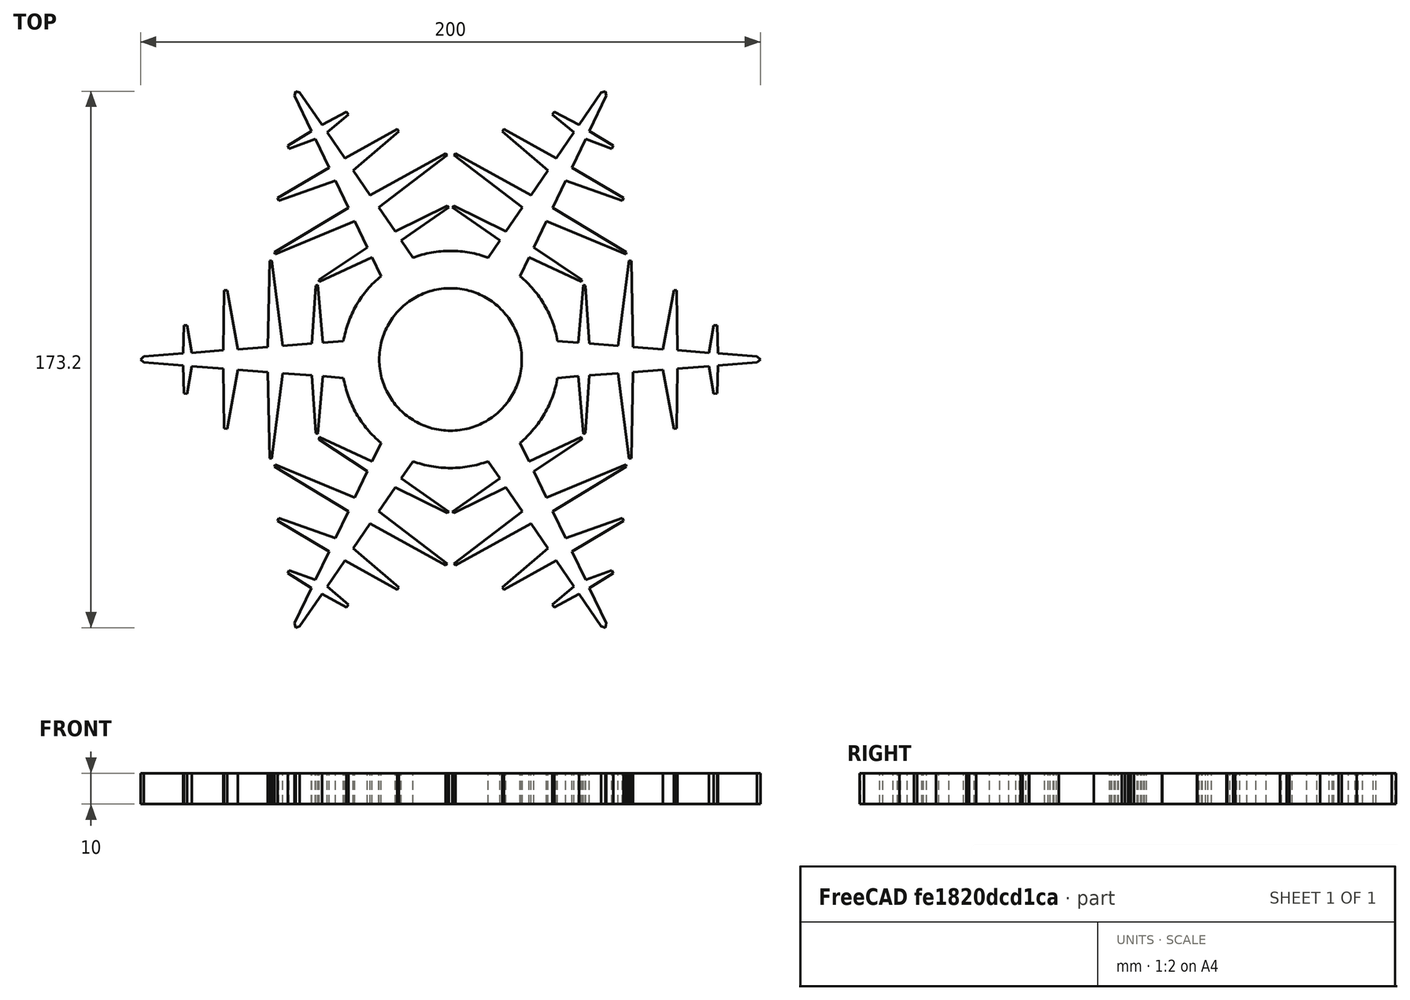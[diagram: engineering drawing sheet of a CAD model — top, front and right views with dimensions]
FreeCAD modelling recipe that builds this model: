
FCSTD DOCUMENT  (FreeCAD 0.17R13541 (Git))
Label: SkiBaskets1
License: All rights reserved
LicenseURL: http://en.wikipedia.org/wiki/All_rights_reserved
objects: Sketcher::SketchObject×1, PartDesign::Pad×1, PartDesign::Mirrored×1, PartDesign::PolarPattern×1, PartDesign::MultiTransform×1, PartDesign::Body×1
note: 7 computed .brp shape members not serialized (recipe doc carries the construction recipe); baked Part::Feature solids carry a one-line shape summary decoded from their .brp

FEATURE [Sketcher::SketchObject] Sketch
  MapMode = 5
  Support = -> [XY_Plane]
  sketch-geometry (25):
    g0: LineSegment [constr] StartX=0 StartY=0 StartZ=0 EndX=60.6218 EndY=35 EndZ=0
    g1: LineSegment [constr] StartX=60.6218 StartY=35 StartZ=0 EndX=100 EndY=0 EndZ=0
    g2: LineSegment StartX=34.54 StartY=5.95197 StartZ=0 EndX=41.2232 EndY=5.43352 EndZ=0
    g3: LineSegment StartX=41.2232 StartY=5.43352 StartZ=0 EndX=42.8555 EndY=24.0849 EndZ=0
    g4: LineSegment StartX=42.8555 StartY=24.0849 StartZ=0 EndX=43.5365 EndY=23.8475 EndZ=0
    g5: LineSegment StartX=43.5365 StartY=23.8475 StartZ=0 EndX=44.7202 EndY=5.16224 EndZ=0
    g6: LineSegment StartX=44.7202 StartY=5.16224 StartZ=0 EndX=54.1123 EndY=4.43366 EndZ=0
    g7: LineSegment StartX=54.1123 StartY=4.43366 StartZ=0 EndX=57.6624 EndY=32.01 EndZ=0
    g8: LineSegment StartX=57.6624 StartY=32.01 StartZ=0 EndX=58.3815 EndY=31.8584 EndZ=0
    g9: LineSegment StartX=58.3815 StartY=31.8584 StartZ=0 EndX=58.9305 EndY=4.05989 EndZ=0
    g10: LineSegment StartX=58.9305 StartY=4.05989 StartZ=0 EndX=68.574 EndY=3.31181 EndZ=0
    g11: LineSegment StartX=68.574 StartY=3.31181 StartZ=0 EndX=72.0968 EndY=22.3422 EndZ=0
    g12: LineSegment StartX=72.0968 StartY=22.3422 StartZ=0 EndX=73.036 EndY=22.2997 EndZ=0
    g13: LineSegment StartX=73.036 StartY=22.2997 StartZ=0 EndX=73.2706 EndY=2.94747 EndZ=0
    g14: LineSegment StartX=73.2706 StartY=2.94747 StartZ=0 EndX=83.4211 EndY=2.16006 EndZ=0
    g15: LineSegment StartX=83.4211 StartY=2.16006 StartZ=0 EndX=84.9667 EndY=11.0606 EndZ=0
    g16: LineSegment StartX=84.9667 StartY=11.0606 StartZ=0 EndX=86.0776 EndY=10.9646 EndZ=0
    g17: LineSegment StartX=86.0776 StartY=10.9646 StartZ=0 EndX=86.3302 EndY=1.93438 EndZ=0
    g18: LineSegment StartX=86.3302 StartY=1.93438 StartZ=0 EndX=98.9227 EndY=0.957527 EndZ=0
    g19: LineSegment StartX=98.9227 StartY=0.957527 StartZ=0 EndX=100 EndY=0 EndZ=0
    g20: LineSegment StartX=100 StartY=0 StartZ=0 EndX=23 EndY=0 EndZ=0
    g21: LineSegment [constr] StartX=30.3743 StartY=6.27512 StartZ=0 EndX=98.9227 EndY=0.957527 EndZ=0
    g22: ArcOfCircle CenterX=0 CenterY=0 CenterZ=0 NormalX=0 NormalY=0 NormalZ=1 AngleXU=0 Radius=23 StartAngle=0 EndAngle=1.5708
    g23: ArcOfCircle CenterX=0 CenterY=0 CenterZ=0 NormalX=0 NormalY=0 NormalZ=1 AngleXU=0 Radius=35.049 StartAngle=0.170645 EndAngle=1.5708
    g24: LineSegment StartX=0 StartY=23 StartZ=0 EndX=0 EndY=35.049 EndZ=0
  constraints (50):
    c: Coincident(g0,g-1)
    c: DistanceX(g-1,g1) = 100
    c: Angle(g-1,g0) = 0.523599
    c: Coincident(g1,g0)
    c: Distance(g0) = 70
    c: Coincident(g3,g2)
    c: Coincident(g4,g3)
    c: Coincident(g5,g4)
    c: Coincident(g6,g5)
    c: Coincident(g7,g6)
    c: Coincident(g8,g7)
    c: Coincident(g9,g8)
    c: Coincident(g10,g9)
    c: Coincident(g12,g11)
    c: Coincident(g13,g12)
    c: Coincident(g14,g13)
    c: Coincident(g15,g14)
    c: Coincident(g16,g15)
    c: Coincident(g17,g16)
    c: Coincident(g18,g17)
    c: Coincident(g19,g18)
    c: Coincident(g21,g18)
    c: PointOnObject(g18,g1)
    c: PointOnObject(g17,g21)
    c: PointOnObject(g14,g21)
    c: PointOnObject(g13,g21)
    c: PointOnObject(g10,g21)
    c: Coincident(g11,g10)
    c: PointOnObject(g9,g21)
    c: PointOnObject(g6,g21)
    c: PointOnObject(g5,g21)
    c: PointOnObject(g2,g21)
    c: PointOnObject(g2,g21)
    c: Equal(g15,g17)
    c: Equal(g13,g11)
    c: Equal(g9,g7)
    c: Equal(g5,g3)
    c: Coincident(g1,g19)
    c: Coincident(g1,g20)
    c: Horizontal(g20)
    c: PointOnObject(g1,g-1)
    c: Coincident(g22,g-1)
    c: PointOnObject(g22,g-2)
    c: PointOnObject(g22,g-1)
    c: Coincident(g23,g-1)
    c: PointOnObject(g23,g-2)
    c: Coincident(g23,g2)
    c: Coincident(g24,g22)
    c: Coincident(g24,g23)
    c: Radius(g22) = 23
FEATURE [PartDesign::Pad] Pad
  Length = 10
  Length2 = 100
  Profile = -> Sketch
  Type = 0
FEATURE [PartDesign::Mirrored] Mirrored
  MirrorPlane = -> Sketch [H_Axis]
FEATURE [PartDesign::PolarPattern] PolarPattern
  Angle = 360
  Axis = -> Sketch [N_Axis]
  Occurrences = 6
FEATURE [PartDesign::MultiTransform] MultiTransform
  BaseFeature = -> Pad
  Originals = -> [Pad]
  Transformations = -> [Mirrored,PolarPattern]
FEATURE [PartDesign::Body] Body
  Group = -> [Sketch,Pad,MultiTransform,Mirrored,PolarPattern]
  Origin = -> Origin
  Tip = -> MultiTransform
